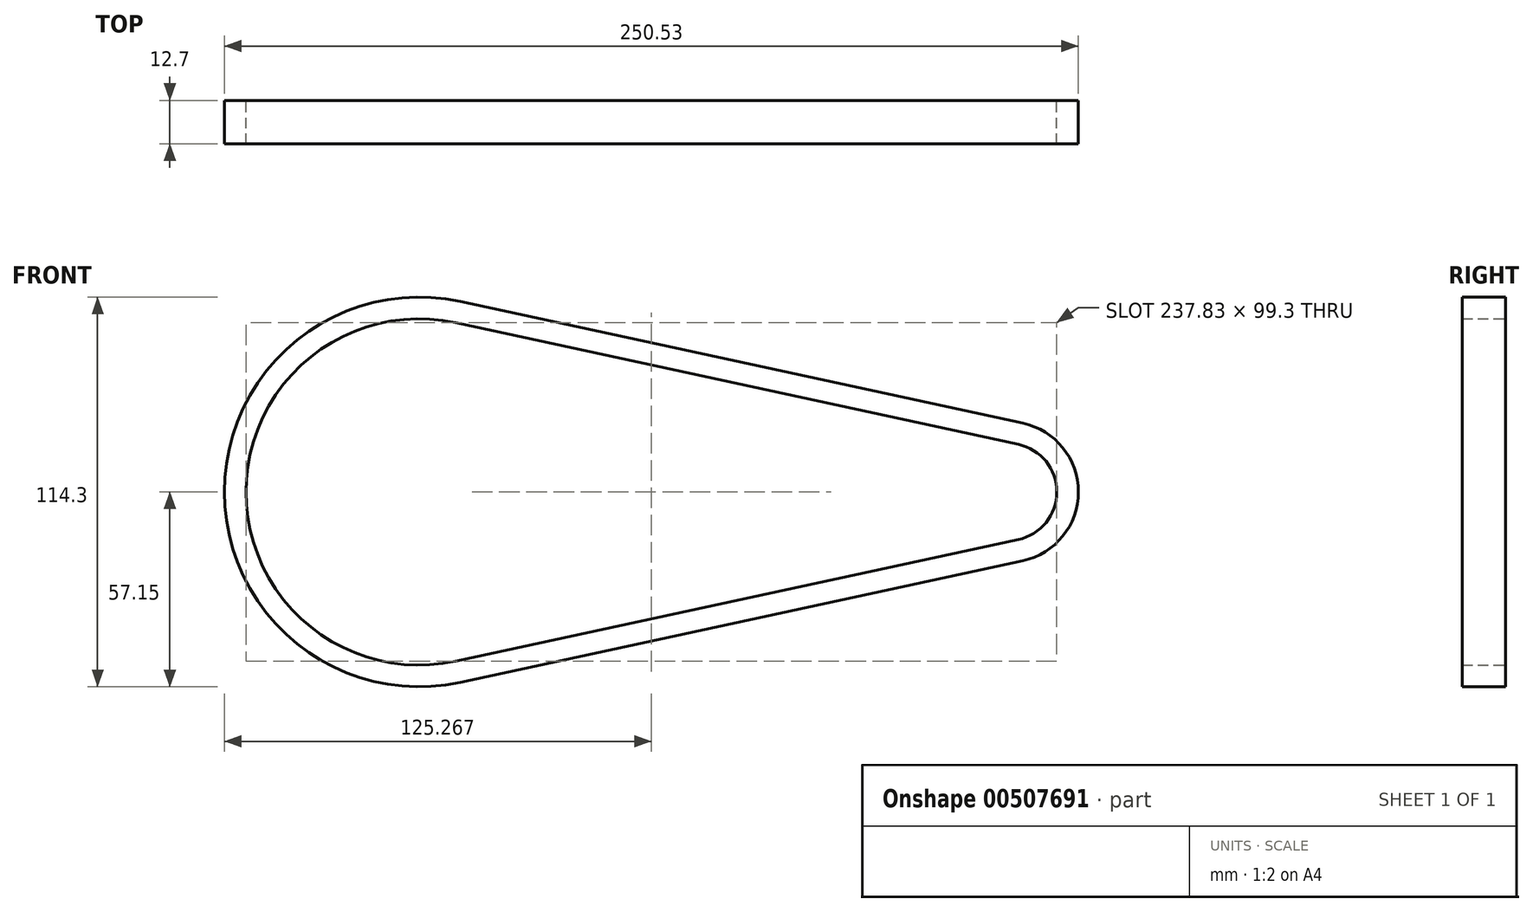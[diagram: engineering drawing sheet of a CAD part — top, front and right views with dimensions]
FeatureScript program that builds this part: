
annotation { "Feature Type Name" : "Feature", "Feature Type Description" : "" }
export const myFeature = defineFeature(function(context is Context, id is Id, definition is map)
    precondition{}
    {
        {
            var Q0;
            Q0=qCreatedBy(makeId("Front.planeOp"),FACE);
            var sketch = newSketch(context, id + "F0", { "sketchPlane" : qUnion([Q0])});
            skArc(sketch, "E0", {"start": v(10.74, 49.65) * mm, "mid": v(-50.8, 0) * mm, "end": v(10.74, -49.65) * mm});
            skArc(sketch, "E1", {"start": v(175.77, -13.96) * mm, "mid": v(187.03, 0) * mm, "end": v(175.77, 13.96) * mm});
            skLineSegment(sketch, "E2", {"start": v(172.75, 0) * mm, "end": v(0, 0) * mm, "construction": true});
            skLineSegment(sketch, "E3", {"start": v(10.74, 49.65) * mm, "end": v(175.77, 13.96) * mm});
            skLineSegment(sketch, "E4.MirrorCS", {"start": v(10.74, -49.65) * mm, "end": v(175.77, -13.96) * mm});
            skArc(sketch, "E5.0", {"start": v(12.08, 55.86) * mm, "mid": v(-57.15, 0) * mm, "end": v(12.08, -55.86) * mm});
            skLineSegment(sketch, "E5.1", {"start": v(12.08, 55.86) * mm, "end": v(177.1, 20.17) * mm});
            skArc(sketch, "E5.2", {"start": v(177.1, -20.17) * mm, "mid": v(193.38, 0) * mm, "end": v(177.1, 20.17) * mm});
            skLineSegment(sketch, "E5.3", {"start": v(12.08, -55.86) * mm, "end": v(177.1, -20.17) * mm});
            skSolve(sketch);
        }
        {
            var Q0;
            Q0=makeQuery(id+"F0.imprint","IMPRINT",FACE,{"disambiguationData":[TD([[makeQuery(id+"F0.imprint","IMPRINT",EDGE,{"derivedFrom":sQuery(id+"F0.wireOp",EDGE,"E0")}),-1.0]])]});
            extrude(context, id + "F1", {"entities" : qUnion([Q0]), "depth" : 12.7 * mm});
        }
    });
